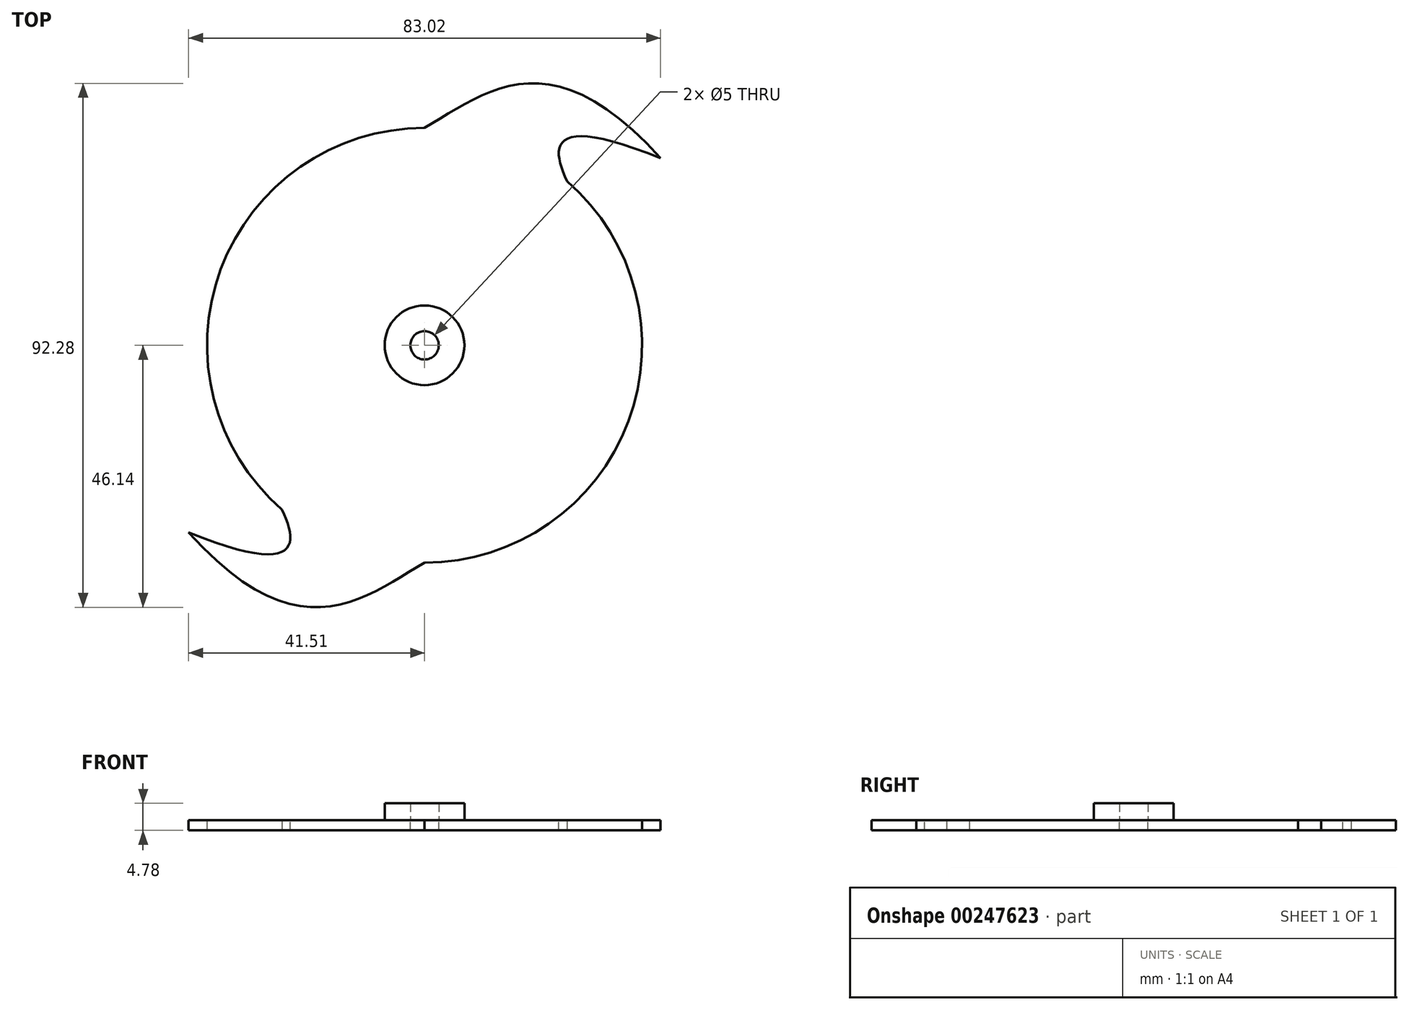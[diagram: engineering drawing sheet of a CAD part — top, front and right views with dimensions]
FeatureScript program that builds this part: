
annotation { "Feature Type Name" : "Feature", "Feature Type Description" : "" }
export const myFeature = defineFeature(function(context is Context, id is Id, definition is map)
    precondition{}
    {
        {
            var Q0;
            Q0=qCreatedBy(makeId("Top.planeOp"),FACE);
            var sketch = newSketch(context, id + "F0", { "sketchPlane" : qUnion([Q0])});
            skCircle(sketch, "E0", {"center": v(0, 0) * mm, "radius": 38.28 * mm});
            skFitSpline(sketch, "E1", {"points": [v(0, 38.28) * mm, v(41.5, 32.95) * mm], "startDerivative": vector(31.58, 18.46) * mm, "endDerivative": vector(58.28, -65.09) * mm});
            skFitSpline(sketch, "E2", {"points": [v(41.5, 32.95) * mm, v(25.07, 28.92) * mm], "startDerivative": vector(-58.28, 23.56) * mm, "endDerivative": vector(8.97, -19) * mm});
            skSolve(sketch);
        }
        {
            var Q0;
            {var subQ0=sQuery(id+"F0.wireOp",EDGE,"E1");Q0=makeQuery(id+"F0.imprint","IMPRINT",FACE,{"disambiguationData":[TD([[makeQuery(id+"F0.imprint","IMPRINT",EDGE,{"derivedFrom":subQ0}),-1.0]])]});}
            var Q1;
            {var subQ0=sQuery(id+"F0.wireOp",EDGE,"E0");var subQ1=makeQuery(id+"F0.imprint","INTERSECT",VERTEX,{"derivedFrom":[sQuery(id+"F0.wireOp",EDGE,"E1"),subQ0]});Q1=makeQuery(id+"F0.imprint","IMPRINT",FACE,{"disambiguationData":[TD([[makeQuery(id+"F0.imprint","IMPRINT",EDGE,{"disambiguationData":[TD([[subQ1,1.0]])],"derivedFrom":subQ0}),1.0]])]});}
            extrude(context, id + "F1", {"entities" : qUnion([Q0, Q1]), "depth" : 1.78 * mm});
        }
        {
            var Q0;
            Q0=makeQuery(id+"F1.opExtrude","SWEPT_BODY",BODY,{"disambiguationData":[OSD([sQuery(id+"F0.wireOp",EDGE,"E1"),sQuery(id+"F0.wireOp",EDGE,"E2"),sQuery(id+"F0.wireOp",EDGE,"E0")])]});
            var Q1;
            Q1=makeQuery(id+"F1.opExtrude","SWEPT_FACE",FACE,{"disambiguationData":[OSD([sQuery(id+"F0.wireOp",EDGE,"E0")])]});
            circularPattern(context, id + "F2", {"operationType" : NewBodyOperationType.ADD, "entities" : qUnion([Q0]), "axis" : qUnion([Q1]), "angle" : 360 * degree, "instanceCount" : 2, "equalSpace" : true});
        }
        {
            var Q0;
            {var subQ0=makeQuery(id+"F1.opExtrude","CAP_FACE",FACE,{"disambiguationData":[OSD([sQuery(id+"F0.wireOp",EDGE,"E1"),sQuery(id+"F0.wireOp",EDGE,"E2"),sQuery(id+"F0.wireOp",EDGE,"E0")])],"isStart":false});Q0=makeQuery(id+"F2.boolean.opBoolean","MERGE",FACE,{"derivedFrom":[subQ0,makeQuery(id+"F2.opPattern","COPY",FACE,{"derivedFrom":subQ0,"instanceName":"1"})]});}
            var sketch = newSketch(context, id + "F3", { "sketchPlane" : qUnion([Q0])});
            skCircle(sketch, "E3", {"center": v(0, 0) * mm, "radius": 2.5 * mm});
            skSolve(sketch);
        }
        {
            var Q0;
            Q0 = qSketchRegion(id + "F3", true);
            extrude(context, id + "F4", {"entities" : qUnion([Q0]), "operationType" : NewBodyOperationType.REMOVE, "oppositeDirection" : true, "depth" : 25 * mm});
        }
        {
            var Q0;
            {var subQ0=makeQuery(id+"F1.opExtrude","CAP_FACE",FACE,{"disambiguationData":[OSD([sQuery(id+"F0.wireOp",EDGE,"E1"),sQuery(id+"F0.wireOp",EDGE,"E2"),sQuery(id+"F0.wireOp",EDGE,"E0")])],"isStart":false});Q0=makeQuery(id+"F2.boolean.opBoolean","MERGE",FACE,{"derivedFrom":[subQ0,makeQuery(id+"F2.opPattern","COPY",FACE,{"derivedFrom":subQ0,"instanceName":"1"})]});}
            var sketch = newSketch(context, id + "F5", { "sketchPlane" : qUnion([Q0])});
            skCircle(sketch, "E4", {"center": v(0, 0) * mm, "radius": 7.02 * mm});
            skCircle(sketch, "E5.0", {"center": v(0, 0) * mm, "radius": 2.5 * mm});
            skSolve(sketch);
        }
        {
            var Q0;
            Q0 = qSketchRegion(id + "F5", true);
            extrude(context, id + "F6", {"entities" : qUnion([Q0]), "depth" : 3 * mm});
        }
    });
